# Revit family: NLRS_57_DUF_UN_9mm_dampdichte_ronde_steekverbinding_LT_velu
name_source: partatom
category: Duct Fittings
units: mm (PartAtom-declared; Revit-internal decimal feet)

## family parameters
Always vertical = Yes
Cut with Voids When Loaded = No
OmniClass Number = 23.75.70.14.14
OmniClass Title = Couplings for Air Ductwork
Part Type = Union
Round Connector Dimension = Use Diameter
Shared = Yes
Work Plane-Based = No

## types (2) — shared parameters
Assembly Code = 57.00
Description = Velu Dampdicht, Ronde steekverbinding
IfcDescription = Velu Dampdicht, Ronde steekverbinding
IfcExportAs = IfcDuctFittingType
IfcExportType = CONNECTOR
Manufacturer = Velu Klimaattechnische groothandel
Model = Velu dampdicht -  ronde steekverbinding
NLRS_C_content_datum_gewijzigd = 16-01-2023
NLRS_C_content_provider = Velu Klimaattechnische groothandel
NLRS_C_content_versie = 3.20.01
Type Comments = Velu Steekverbinding
URL = https://webshop.velu.nl
VELU_Article_Data = Steekverbinding dampdicht
zero-valued in all types: Default Elevation

## type names (no varying parameters)
- Standard
- SN

## geometry (parser evidence)
native form markers: Sweep x7
no freeform markers — native parametric forms only
